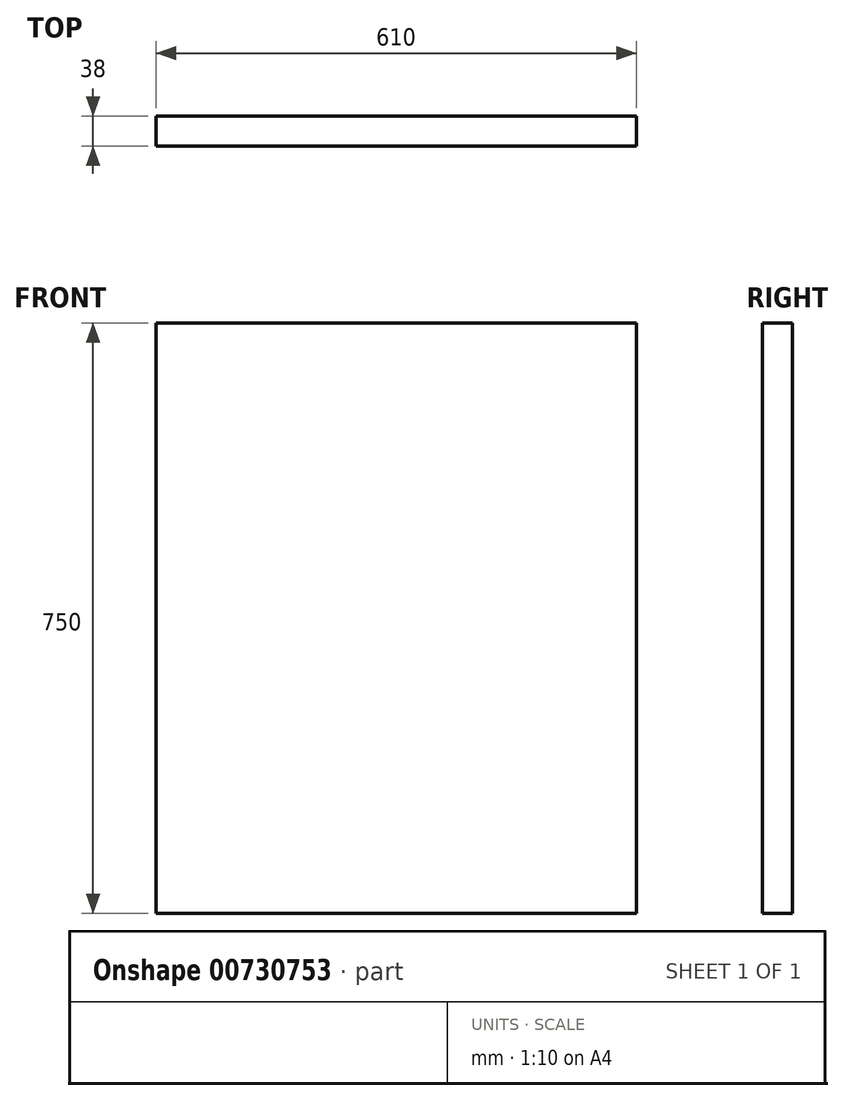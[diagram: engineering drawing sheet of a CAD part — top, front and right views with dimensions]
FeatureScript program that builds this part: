
annotation { "Feature Type Name" : "Feature", "Feature Type Description" : "" }
export const myFeature = defineFeature(function(context is Context, id is Id, definition is map)
    precondition{}
    {
        {
            var Q0;
            Q0=qCreatedBy(makeId("Front.planeOp"),FACE);
            var sketch = newSketch(context, id + "F0", { "sketchPlane" : qUnion([Q0])});
            skLineSegment(sketch, "E0.bottom", {"start": v(-305, 375) * mm, "end": v(305, 375) * mm});
            skLineSegment(sketch, "E0.top", {"start": v(-305, -375) * mm, "end": v(305, -375) * mm});
            skLineSegment(sketch, "E0.left", {"start": v(-305, 375) * mm, "end": v(-305, -375) * mm});
            skLineSegment(sketch, "E0.right", {"start": v(305, 375) * mm, "end": v(305, -375) * mm});
            skPoint(sketch, "E0.middle", {"position": v(0, 0) * mm});
            skSolve(sketch);
        }
        {
            var Q0;
            Q0 = qSketchRegion(id + "F0", true);
            extrude(context, id + "F1", {"entities" : qUnion([Q0]), "endBound" : BoundingType.SYMMETRIC, "depth" : 38 * mm, "offsetDistance" : 25.4 * mm});
        }
    });
